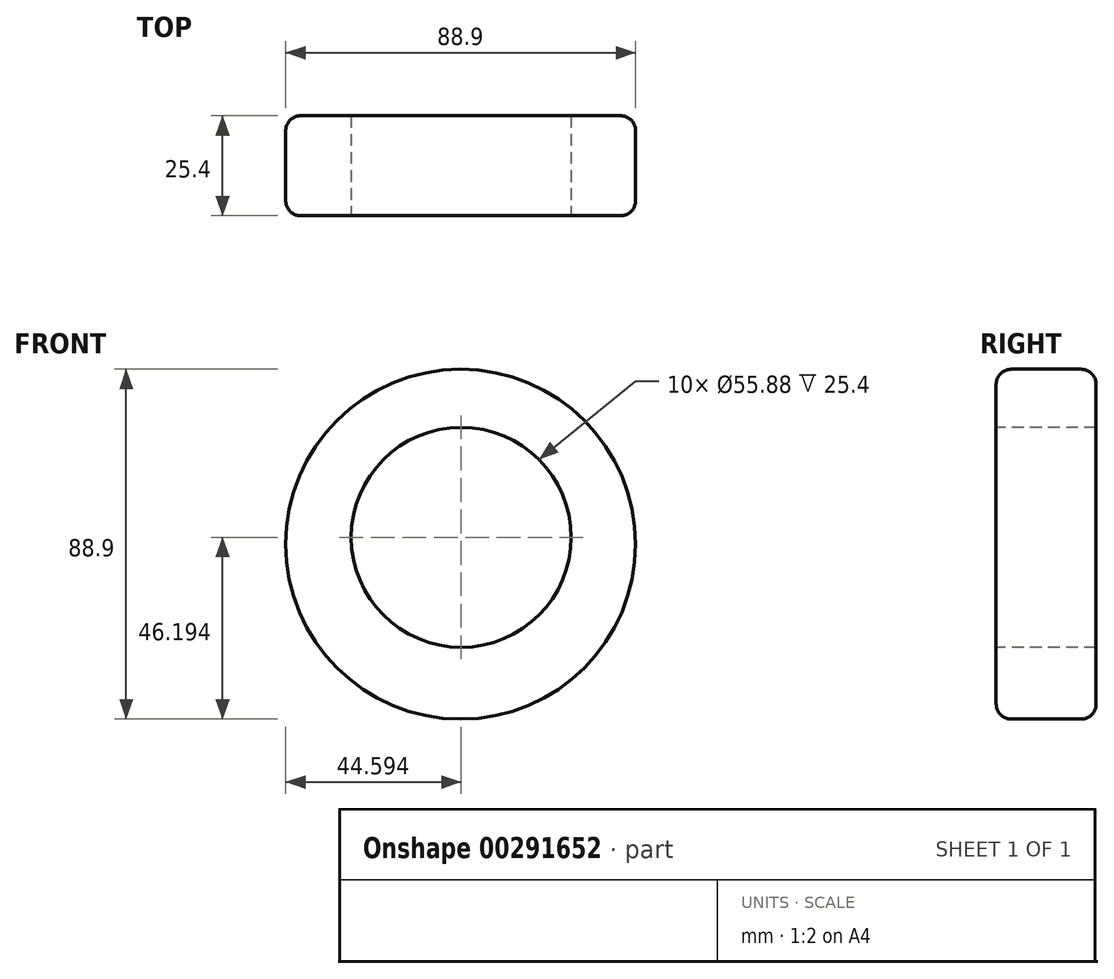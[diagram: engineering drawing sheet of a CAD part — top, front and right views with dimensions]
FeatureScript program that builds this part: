
annotation { "Feature Type Name" : "Feature", "Feature Type Description" : "" }
export const myFeature = defineFeature(function(context is Context, id is Id, definition is map)
    precondition{}
    {
        {
            var Q0;
            Q0=qCreatedBy(makeId("Front.planeOp"),FACE);
            var sketch = newSketch(context, id + "F0", { "sketchPlane" : qUnion([Q0])});
            skCircle(sketch, "E0", {"center": v(30.44, -5.72) * mm, "radius": 44.45 * mm});
            skPoint(sketch, "E0.first.point", {"position": v(-12.67, 5.11) * mm});
            skPoint(sketch, "E0.second.point", {"position": v(61.57, 26) * mm});
            skPoint(sketch, "E0.third.point", {"position": v(0, 26.67) * mm});
            skSolve(sketch);
        }
        {
            var Q0;
            Q0=makeQuery(id+"F0.imprint","IMPRINT",FACE,{"disambiguationData":[TD([[makeQuery(id+"F0.imprint","IMPRINT",EDGE,{"derivedFrom":sQuery(id+"F0.wireOp",EDGE,"E0")}),1.0]])]});
            extrude(context, id + "F1", {"entities" : qUnion([Q0]), "endBound" : BoundingType.SYMMETRIC, "depth" : 25.4 * mm});
        }
        {
            var Q0;
            Q0=makeQuery(id+"F1.opExtrude","CAP_EDGE",EDGE,{"disambiguationData":[OSD([sQuery(id+"F0.wireOp",EDGE,"E0")])],"isStart":false});
            var Q1;
            Q1=makeQuery(id+"F1.opExtrude","CAP_EDGE",EDGE,{"disambiguationData":[OSD([sQuery(id+"F0.wireOp",EDGE,"E0")])],"isStart":true});
            fillet(context, id + "F2", {"entities" : qUnion([Q0, Q1]), "radius" : 3.8 * mm, "tangentPropagation" : true, "allowEdgeOverflow" : false});
        }
        {
            var Q0;
            Q0=makeQuery(id+"F1.opExtrude","CAP_FACE",FACE,{"disambiguationData":[OSD([sQuery(id+"F0.wireOp",EDGE,"E0")])],"isStart":false});
            var sketch = newSketch(context, id + "F3", { "sketchPlane" : qUnion([Q0])});
            skCircle(sketch, "E1", {"center": v(30.58, -3.98) * mm, "radius": 27.94 * mm});
            skPoint(sketch, "E1.first.point", {"position": v(8.99, -21.7) * mm});
            skPoint(sketch, "E1.second.point", {"position": v(52.58, 13.26) * mm});
            skPoint(sketch, "E1.third.point", {"position": v(16.07, 19.9) * mm});
            skSolve(sketch);
        }
        {
            var Q0;
            Q0=makeQuery(id+"F3.imprint","IMPRINT",FACE,{"disambiguationData":[TD([[makeQuery(id+"F3.imprint","IMPRINT",EDGE,{"derivedFrom":sQuery(id+"F3.wireOp",EDGE,"E1")}),1.0]])]});
            extrude(context, id + "F4", {"entities" : qUnion([Q0]), "operationType" : NewBodyOperationType.REMOVE, "endBound" : BoundingType.THROUGH_ALL, "oppositeDirection" : true, "depth" : 25.4 * mm});
        }
    });
